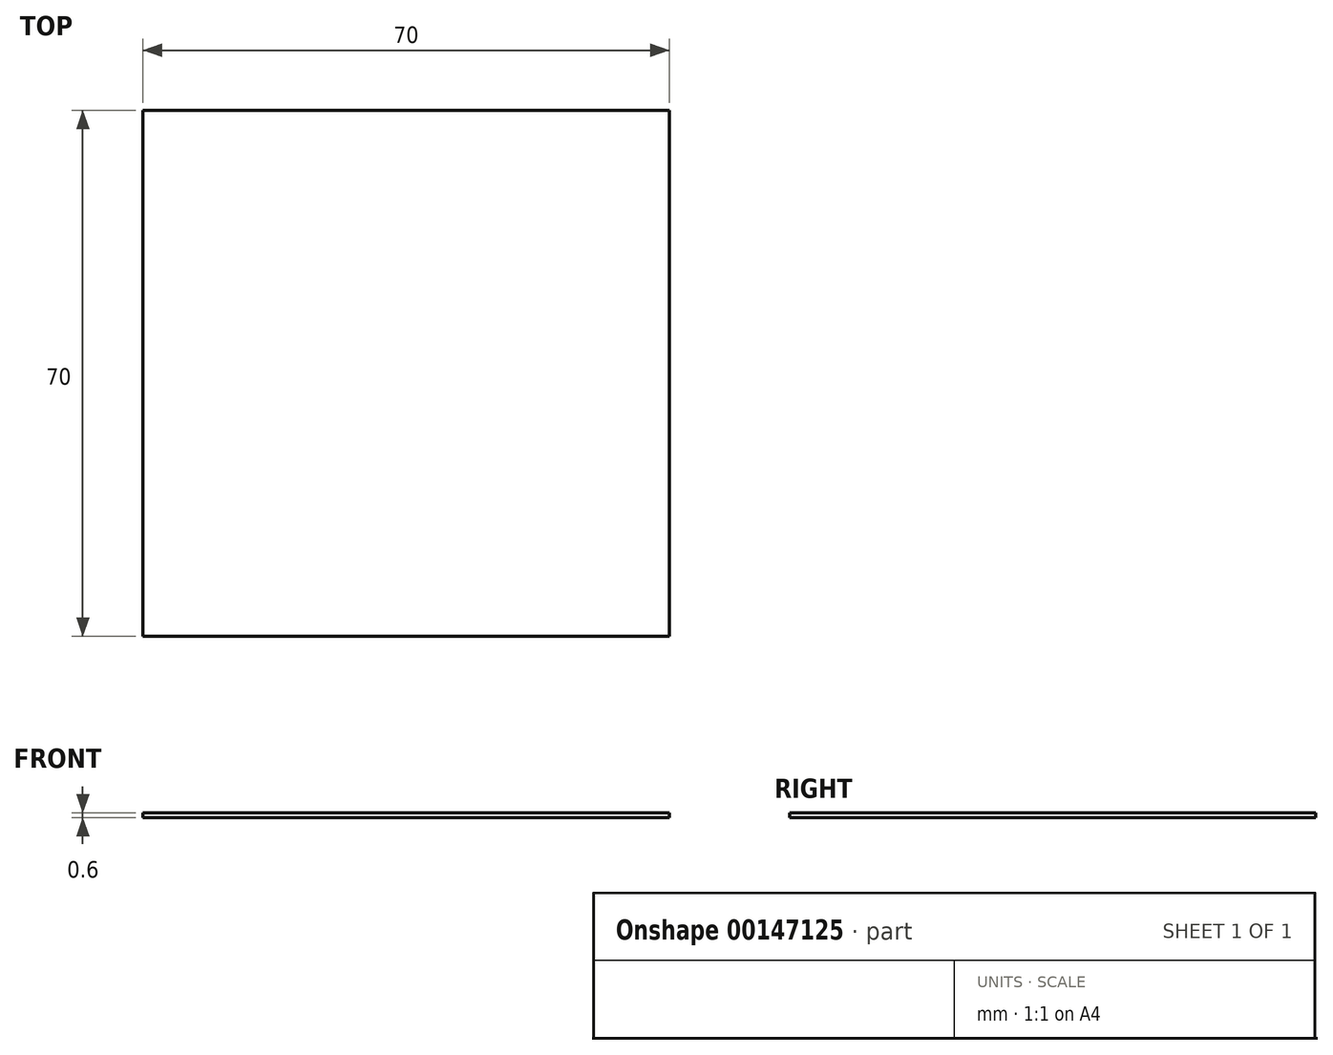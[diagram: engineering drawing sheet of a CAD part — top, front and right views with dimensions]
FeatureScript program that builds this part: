
annotation { "Feature Type Name" : "Feature", "Feature Type Description" : "" }
export const myFeature = defineFeature(function(context is Context, id is Id, definition is map)
    precondition{}
    {
        {
            var Q0;
            Q0=qCreatedBy(makeId("Top.planeOp"),FACE);
            var sketch = newSketch(context, id + "F0", { "sketchPlane" : qUnion([Q0])});
            skLineSegment(sketch, "E0.bottom", {"start": v(35, 35) * mm, "end": v(-35, 35) * mm});
            skLineSegment(sketch, "E0.top", {"start": v(35, -35) * mm, "end": v(-35, -35) * mm});
            skLineSegment(sketch, "E0.left", {"start": v(35, 35) * mm, "end": v(35, -35) * mm});
            skLineSegment(sketch, "E0.right", {"start": v(-35, 35) * mm, "end": v(-35, -35) * mm});
            skPoint(sketch, "E0.middle", {"position": v(0, 0) * mm});
            skSolve(sketch);
        }
        {
            var Q0;
            Q0=makeQuery(id+"F0.imprint","IMPRINT",FACE,{"disambiguationData":[TD([[makeQuery(id+"F0.imprint","IMPRINT",EDGE,{"derivedFrom":sQuery(id+"F0.wireOp",EDGE,"E0.bottom")}),1.0]])]});
            extrude(context, id + "F1", {"entities" : qUnion([Q0]), "depth" : 0.6 * mm});
        }
    });
